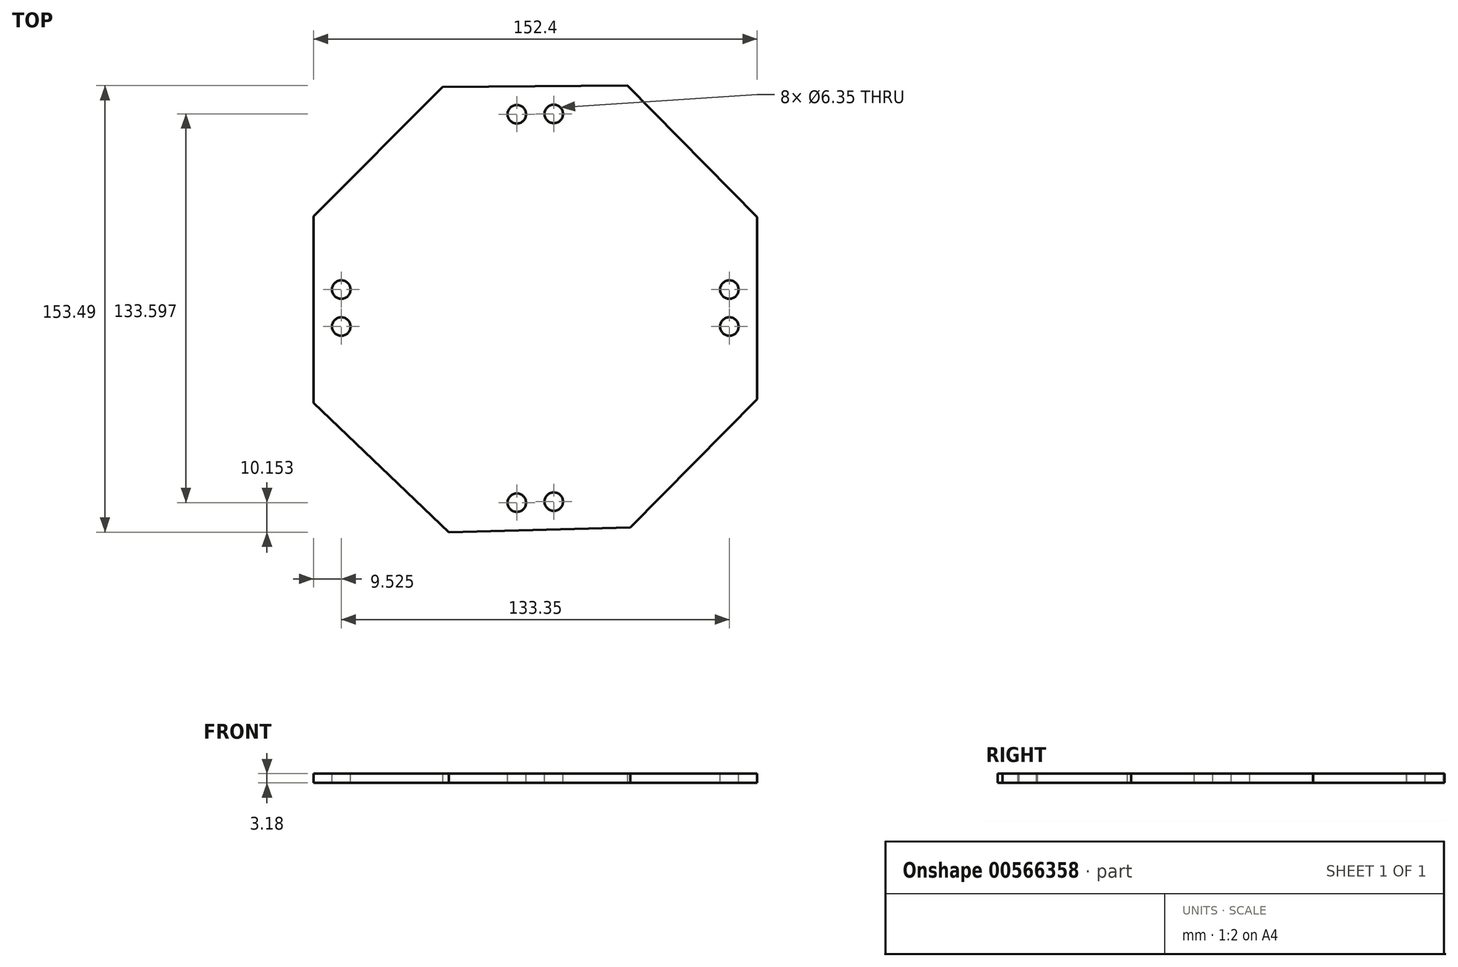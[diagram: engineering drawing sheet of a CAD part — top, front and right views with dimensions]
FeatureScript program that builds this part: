
annotation { "Feature Type Name" : "Feature", "Feature Type Description" : "" }
export const myFeature = defineFeature(function(context is Context, id is Id, definition is map)
    precondition{}
    {
        {
            var Q0;
            Q0=qCreatedBy(makeId("Top.planeOp"),FACE);
            var sketch = newSketch(context, id + "F0", { "sketchPlane" : qUnion([Q0])});
            skCircle(sketch, "E0.cCircle", {"center": v(0, 0) * mm, "radius": 76.2 * mm, "construction": true});
            skLineSegment(sketch, "E0.0", {"start": v(76.2, 31.27) * mm, "end": v(76.2, -31.27) * mm});
            skLineSegment(sketch, "E0.1", {"start": v(76.2, -31.27) * mm, "end": v(32.7, -75.36) * mm});
            skLineSegment(sketch, "E0.2", {"start": v(32.7, -75.36) * mm, "end": v(-29.72, -77.02) * mm});
            skLineSegment(sketch, "E0.3", {"start": v(-29.72, -77.02) * mm, "end": v(-76.2, -32.57) * mm});
            skLineSegment(sketch, "E0.4", {"start": v(-76.2, -32.57) * mm, "end": v(-76.2, 31.49) * mm});
            skLineSegment(sketch, "E0.5", {"start": v(-76.2, 31.49) * mm, "end": v(-31.9, 75.94) * mm});
            skLineSegment(sketch, "E0.6", {"start": v(-31.9, 75.94) * mm, "end": v(31.6, 76.47) * mm});
            skLineSegment(sketch, "E0.7", {"start": v(31.6, 76.47) * mm, "end": v(76.2, 31.27) * mm});
            skPoint(sketch, "E0.0.midPoint", {"position": v(76.2, 0) * mm});
            skSolve(sketch);
        }
        {
            var Q0;
            Q0 = qSketchRegion(id + "F0", true);
            extrude(context, id + "F1", {"entities" : qUnion([Q0]), "depth" : 3.17 * mm, "offsetDistance" : 25.4 * mm, "symmetric" : true});
        }
        {
            var Q0;
            Q0=makeQuery(id+"F1.opExtrude","CAP_FACE",FACE,{"disambiguationData":[OSD([sQuery(id+"F0.wireOp",EDGE,"E0.0"),sQuery(id+"F0.wireOp",EDGE,"E0.1"),sQuery(id+"F0.wireOp",EDGE,"E0.2"),sQuery(id+"F0.wireOp",EDGE,"E0.3"),sQuery(id+"F0.wireOp",EDGE,"E0.4"),sQuery(id+"F0.wireOp",EDGE,"E0.5"),sQuery(id+"F0.wireOp",EDGE,"E0.6"),sQuery(id+"F0.wireOp",EDGE,"E0.7")])],"isStart":false});
            var sketch = newSketch(context, id + "F2", { "sketchPlane" : qUnion([Q0])});
            skCircle(sketch, "E1", {"center": v(-6.35, 66.62) * mm, "radius": 3.18 * mm});
            skCircle(sketch, "E2", {"center": v(6.35, 66.73) * mm, "radius": 3.18 * mm});
            skCircle(sketch, "E3", {"center": v(66.67, 6.35) * mm, "radius": 3.18 * mm});
            skCircle(sketch, "E4", {"center": v(66.67, -6.35) * mm, "radius": 3.18 * mm});
            skCircle(sketch, "E5", {"center": v(6.35, -66.53) * mm, "radius": 3.18 * mm});
            skCircle(sketch, "E6", {"center": v(-6.35, -66.87) * mm, "radius": 3.18 * mm});
            skCircle(sketch, "E7", {"center": v(-66.67, -6.35) * mm, "radius": 3.18 * mm});
            skCircle(sketch, "E8", {"center": v(-66.67, 6.35) * mm, "radius": 3.18 * mm});
            skSolve(sketch);
        }
        {
            var Q0;
            Q0=makeQuery(id+"F2.imprint","IMPRINT",FACE,{"disambiguationData":[TD([[makeQuery(id+"F2.imprint","IMPRINT",EDGE,{"derivedFrom":sQuery(id+"F2.wireOp",EDGE,"E8")}),1.0]])]});
            var Q1;
            Q1=makeQuery(id+"F2.imprint","IMPRINT",FACE,{"disambiguationData":[TD([[makeQuery(id+"F2.imprint","IMPRINT",EDGE,{"derivedFrom":sQuery(id+"F2.wireOp",EDGE,"E7")}),1.0]])]});
            var Q2;
            Q2=makeQuery(id+"F2.imprint","IMPRINT",FACE,{"disambiguationData":[TD([[makeQuery(id+"F2.imprint","IMPRINT",EDGE,{"derivedFrom":sQuery(id+"F2.wireOp",EDGE,"E5")}),1.0]])]});
            var Q3;
            Q3=makeQuery(id+"F2.imprint","IMPRINT",FACE,{"disambiguationData":[TD([[makeQuery(id+"F2.imprint","IMPRINT",EDGE,{"derivedFrom":sQuery(id+"F2.wireOp",EDGE,"E6")}),1.0]])]});
            var Q4;
            Q4=makeQuery(id+"F2.imprint","IMPRINT",FACE,{"disambiguationData":[TD([[makeQuery(id+"F2.imprint","IMPRINT",EDGE,{"derivedFrom":sQuery(id+"F2.wireOp",EDGE,"E4")}),1.0]])]});
            var Q5;
            Q5=makeQuery(id+"F2.imprint","IMPRINT",FACE,{"disambiguationData":[TD([[makeQuery(id+"F2.imprint","IMPRINT",EDGE,{"derivedFrom":sQuery(id+"F2.wireOp",EDGE,"E3")}),1.0]])]});
            var Q6;
            Q6=makeQuery(id+"F2.imprint","IMPRINT",FACE,{"disambiguationData":[TD([[makeQuery(id+"F2.imprint","IMPRINT",EDGE,{"derivedFrom":sQuery(id+"F2.wireOp",EDGE,"E2")}),1.0]])]});
            var Q7;
            Q7=makeQuery(id+"F2.imprint","IMPRINT",FACE,{"disambiguationData":[TD([[makeQuery(id+"F2.imprint","IMPRINT",EDGE,{"derivedFrom":sQuery(id+"F2.wireOp",EDGE,"E1")}),1.0]])]});
            extrude(context, id + "F3", {"entities" : qUnion([Q0, Q1, Q2, Q3, Q4, Q5, Q6, Q7]), "operationType" : NewBodyOperationType.REMOVE, "endBound" : BoundingType.THROUGH_ALL, "oppositeDirection" : true, "depth" : 25.4 * mm, "offsetDistance" : 25.4 * mm});
        }
    });
